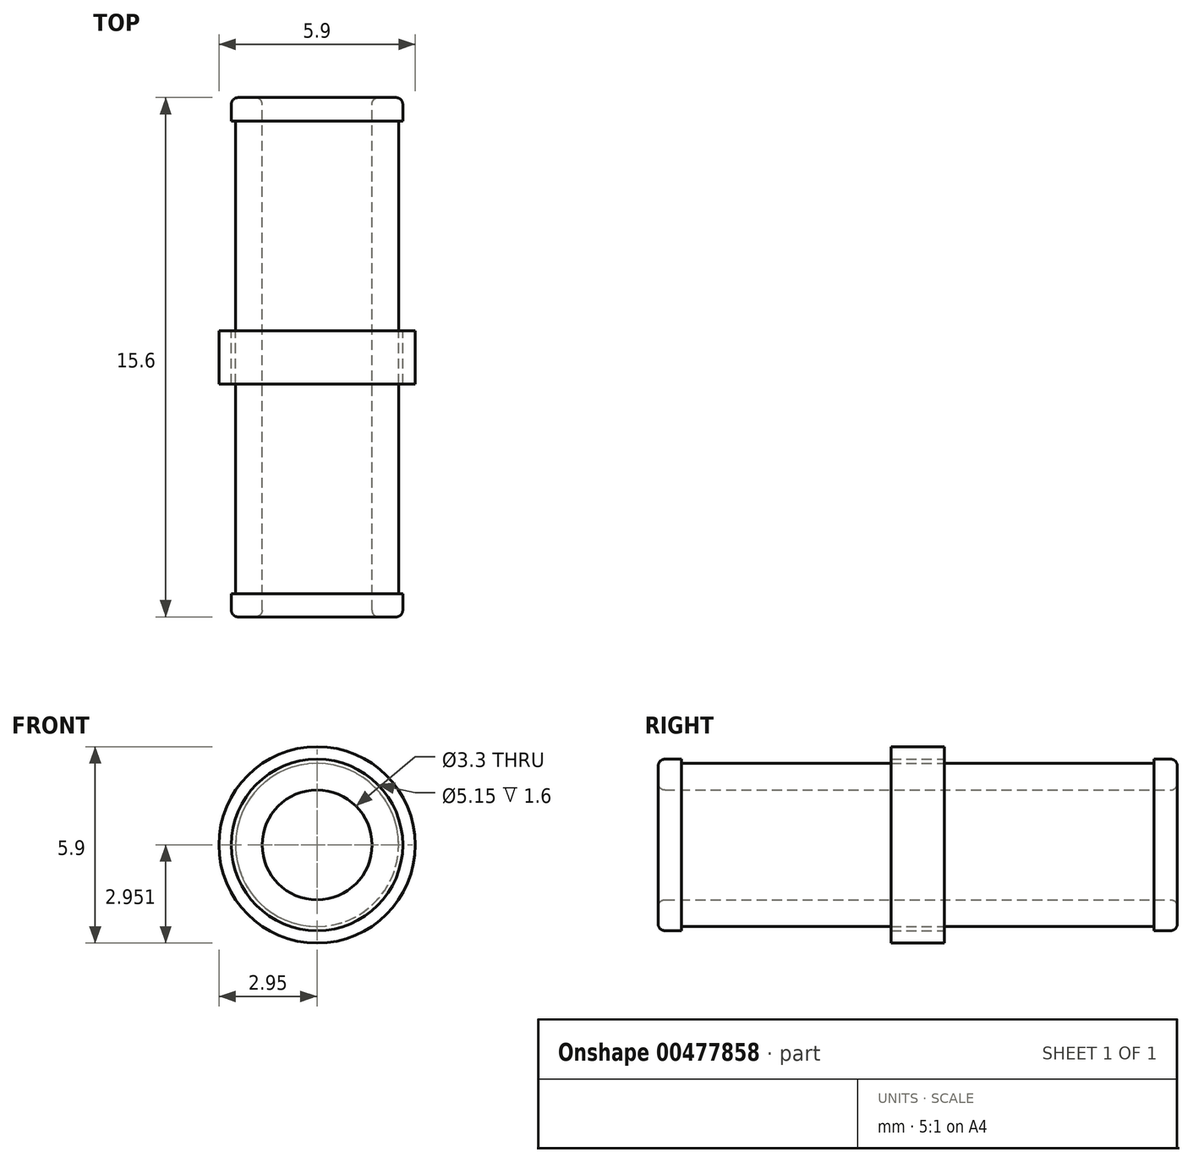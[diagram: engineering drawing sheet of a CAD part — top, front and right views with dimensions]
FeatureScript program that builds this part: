
annotation { "Feature Type Name" : "Feature", "Feature Type Description" : "" }
export const myFeature = defineFeature(function(context is Context, id is Id, definition is map)
    precondition{}
    {
        {
            var Q0;
            Q0=qCreatedBy(makeId("Front.planeOp"),FACE);
            var sketch = newSketch(context, id + "F0", { "sketchPlane" : qUnion([Q0])});
            skCircle(sketch, "E0", {"center": v(-40.37, 25.87) * mm, "radius": 2.95 * mm});
            skCircle(sketch, "E1", {"center": v(-40.37, 25.87) * mm, "radius": 2.45 * mm});
            skCircle(sketch, "E2", {"center": v(-40.37, 25.87) * mm, "radius": 1.65 * mm});
            skCircle(sketch, "E3", {"center": v(-40.37, 25.87) * mm, "radius": 2.58 * mm});
            skSolve(sketch);
        }
        {
            var Q0;
            Q0=makeQuery(id+"F0.imprint","IMPRINT",FACE,{"disambiguationData":[TD([[makeQuery(id+"F0.imprint","IMPRINT",EDGE,{"derivedFrom":sQuery(id+"F0.wireOp",EDGE,"E0")}),1.0]])]});
            extrude(context, id + "F1", {"entities" : qUnion([Q0]), "depth" : 0.8 * mm, "offsetDistance" : 25 * mm});
        }
        {
            var Q0;
            Q0=makeQuery(id+"F0.imprint","IMPRINT",FACE,{"disambiguationData":[TD([[makeQuery(id+"F0.imprint","IMPRINT",EDGE,{"derivedFrom":sQuery(id+"F0.wireOp",EDGE,"E1")}),-1.0]])]});
            extrude(context, id + "F2", {"entities" : qUnion([Q0]), "operationType" : NewBodyOperationType.ADD, "depth" : 0.8 * mm, "offsetDistance" : 25 * mm});
        }
        {
            var Q0;
            Q0=makeQuery(id+"F0.imprint","IMPRINT",FACE,{"disambiguationData":[TD([[makeQuery(id+"F0.imprint","IMPRINT",EDGE,{"derivedFrom":sQuery(id+"F0.wireOp",EDGE,"E1")}),1.0]])]});
            extrude(context, id + "F3", {"entities" : qUnion([Q0]), "operationType" : NewBodyOperationType.ADD, "depth" : 7.8 * mm, "offsetDistance" : 25 * mm});
        }
        {
            var Q0;
            Q0=makeQuery(id+"F0.imprint","IMPRINT",FACE,{"disambiguationData":[TD([[makeQuery(id+"F0.imprint","IMPRINT",EDGE,{"derivedFrom":sQuery(id+"F0.wireOp",EDGE,"E1")}),-1.0]])]});
            extrude(context, id + "F4", {"entities" : qUnion([Q0]), "depth" : 7.8 * mm, "offsetDistance" : 25 * mm});
        }
        {
            var Q0;
            Q0=makeQuery(id+"F0.imprint","IMPRINT",FACE,{"disambiguationData":[TD([[makeQuery(id+"F0.imprint","IMPRINT",EDGE,{"derivedFrom":sQuery(id+"F0.wireOp",EDGE,"E1")}),-1.0]])]});
            extrude(context, id + "F5", {"entities" : qUnion([Q0]), "operationType" : NewBodyOperationType.REMOVE, "depth" : 7.1 * mm, "offsetDistance" : 25 * mm});
        }
        {
            var Q0;
            Q0=makeQuery(id+"F0.imprint","IMPRINT",FACE,{"disambiguationData":[TD([[makeQuery(id+"F0.imprint","IMPRINT",EDGE,{"derivedFrom":sQuery(id+"F0.wireOp",EDGE,"E1")}),1.0]])]});
            extrude(context, id + "F6", {"entities" : qUnion([Q0]), "operationType" : NewBodyOperationType.ADD, "oppositeDirection" : true, "depth" : 7.8 * mm, "offsetDistance" : 25 * mm});
        }
        {
            var Q0;
            Q0=makeQuery(id+"F0.imprint","IMPRINT",FACE,{"disambiguationData":[TD([[makeQuery(id+"F0.imprint","IMPRINT",EDGE,{"derivedFrom":sQuery(id+"F0.wireOp",EDGE,"E0")}),1.0]])]});
            extrude(context, id + "F7", {"entities" : qUnion([Q0]), "operationType" : NewBodyOperationType.ADD, "oppositeDirection" : true, "depth" : 0.8 * mm, "offsetDistance" : 25 * mm});
        }
        {
            var Q0;
            Q0=makeQuery(id+"F4.opExtrude","SWEPT_BODY",BODY,{"disambiguationData":[OSD([sQuery(id+"F0.wireOp",EDGE,"E1"),sQuery(id+"F0.wireOp",EDGE,"E3")])]});
            var Q1;
            Q1=makeQuery(id+"F2.opExtrude","SWEPT_BODY",BODY,{"disambiguationData":[OSD([sQuery(id+"F0.wireOp",EDGE,"E1"),sQuery(id+"F0.wireOp",EDGE,"E3")])]});
            var Q2;
            Q2=makeQuery(id+"F1.opExtrude","SWEPT_BODY",BODY,{"disambiguationData":[OSD([sQuery(id+"F0.wireOp",EDGE,"E0"),sQuery(id+"F0.wireOp",EDGE,"E3")])]});
            var Q3;
            Q3=qCreatedBy(makeId("Front.planeOp"),FACE);
            mirror(context, id + "F8", {"operationType" : NewBodyOperationType.ADD, "entities" : qUnion([Q0, Q1, Q2]), "mirrorPlane" : qUnion([Q3])});
        }
        {
            var Q0;
            Q0=makeQuery(id+"F3.opExtrude","CAP_EDGE",EDGE,{"disambiguationData":[OSD([sQuery(id+"F0.wireOp",EDGE,"E2")])],"isStart":false});
            var Q1;
            Q1=makeQuery(id+"F4.opExtrude","CAP_EDGE",EDGE,{"disambiguationData":[OSD([sQuery(id+"F0.wireOp",EDGE,"E3")])],"isStart":false});
            var Q2;
            Q2=makeQuery(id+"F5.boolean.opBoolean","COPY",EDGE,{"derivedFrom":makeQuery(id+"F5.opExtrude","CAP_EDGE",EDGE,{"disambiguationData":[OSD([sQuery(id+"F0.wireOp",EDGE,"E3")])],"isStart":false})});
            var Q3;
            Q3=makeQuery(id+"F8.opPattern","COPY",EDGE,{"derivedFrom":makeQuery(id+"F4.opExtrude","CAP_EDGE",EDGE,{"disambiguationData":[OSD([sQuery(id+"F0.wireOp",EDGE,"E3")])],"isStart":false}),"instanceName":"1"});
            var Q4;
            Q4=makeQuery(id+"F8.opPattern","COPY",EDGE,{"derivedFrom":makeQuery(id+"F5.boolean.opBoolean","COPY",EDGE,{"derivedFrom":makeQuery(id+"F5.opExtrude","CAP_EDGE",EDGE,{"disambiguationData":[OSD([sQuery(id+"F0.wireOp",EDGE,"E3")])],"isStart":false})}),"instanceName":"1"});
            var Q5;
            Q5=makeQuery(id+"F6.opExtrude","CAP_EDGE",EDGE,{"disambiguationData":[OSD([sQuery(id+"F0.wireOp",EDGE,"E2")])],"isStart":false});
            fillet(context, id + "F9", {"entities" : qUnion([Q0, Q1, Q2, Q3, Q4, Q5]), "radius" : 0.2 * mm, "tangentPropagation" : true, "allowEdgeOverflow" : false});
        }
    });
